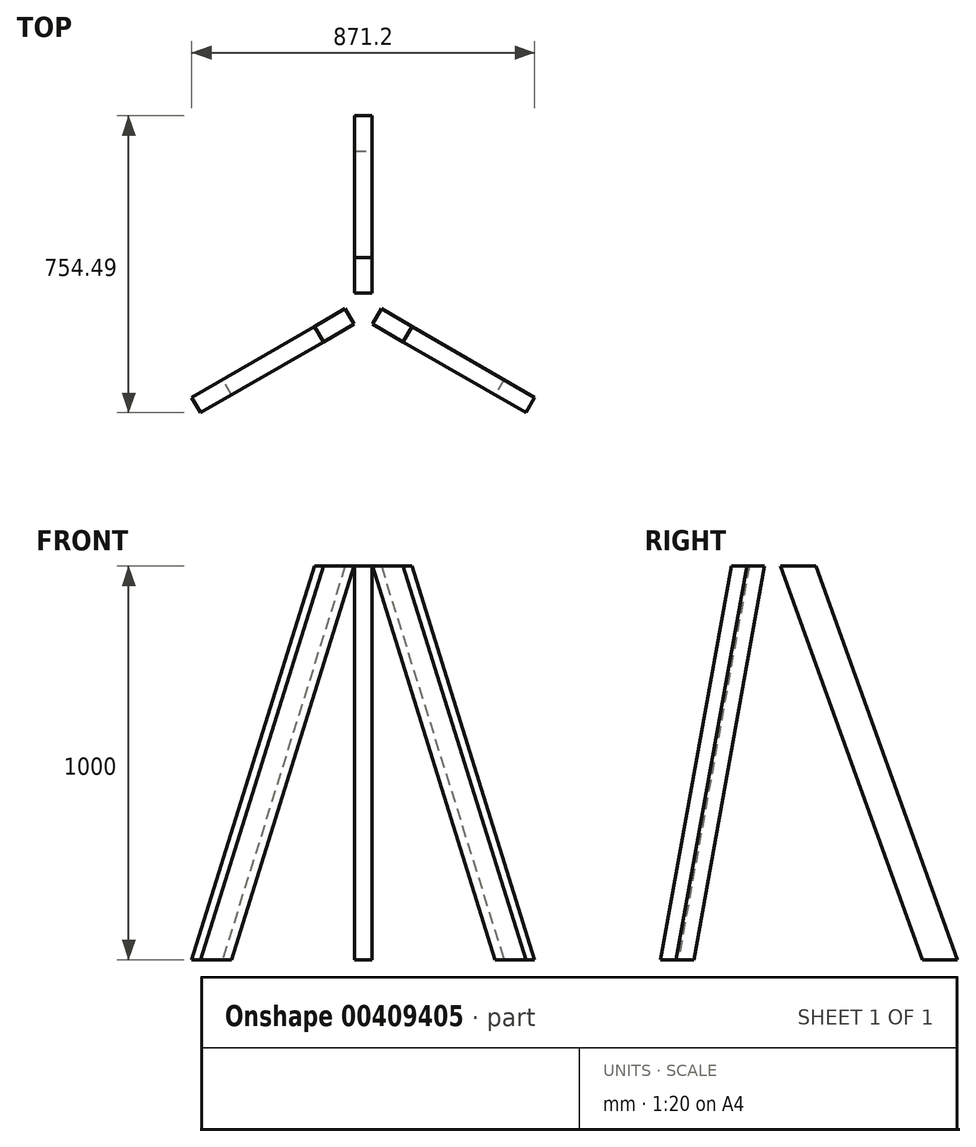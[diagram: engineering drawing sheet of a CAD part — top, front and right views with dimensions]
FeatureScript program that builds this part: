
annotation { "Feature Type Name" : "Feature", "Feature Type Description" : "" }
export const myFeature = defineFeature(function(context is Context, id is Id, definition is map)
    precondition{}
    {
        {
            var Q0;
            Q0=qCreatedBy(makeId("Top.planeOp"),FACE);
            cPlane(context, id + "F0", {"entities" : qUnion([Q0]), "cplaneType" : CPlaneType.OFFSET, "offset" : 25 * mm, "width" : 150 * mm, "height" : 150 * mm});
        }
        {
            var Q0;
            Q0=qCreatedBy(id+"F0.planeOp",FACE);
            var sketch = newSketch(context, id + "F1", { "sketchPlane" : qUnion([Q0])});
            skLineSegment(sketch, "E0.bottom", {"start": v(-22.5, 490) * mm, "end": v(22.5, 490) * mm});
            skLineSegment(sketch, "E0.top", {"start": v(-22.5, 400) * mm, "end": v(22.5, 400) * mm});
            skLineSegment(sketch, "E0.left", {"start": v(-22.5, 490) * mm, "end": v(-22.5, 400) * mm});
            skLineSegment(sketch, "E0.right", {"start": v(22.5, 490) * mm, "end": v(22.5, 400) * mm});
            skLineSegment(sketch, "E1", {"start": v(0, 0) * mm, "end": v(0, 1012.22) * mm, "construction": true});
            skPoint(sketch, "E2.center", {"position": v(0, 506.11) * mm});
            skLineSegment(sketch, "E3.1.0", {"start": v(-435.6, -225.51) * mm, "end": v(-357.66, -180.51) * mm});
            skLineSegment(sketch, "E3.1.1", {"start": v(-413.1, -264.49) * mm, "end": v(-335.16, -219.49) * mm});
            skLineSegment(sketch, "E3.1.2", {"start": v(-413.1, -264.49) * mm, "end": v(-435.6, -225.51) * mm});
            skLineSegment(sketch, "E3.1.3", {"start": v(-335.16, -219.49) * mm, "end": v(-357.66, -180.51) * mm});
            skLineSegment(sketch, "E3.1.4", {"start": v(0, 0) * mm, "end": v(-876.61, -506.11) * mm, "construction": true});
            skLineSegment(sketch, "E3.2.0", {"start": v(413.1, -264.49) * mm, "end": v(335.16, -219.49) * mm});
            skLineSegment(sketch, "E3.2.1", {"start": v(435.6, -225.51) * mm, "end": v(357.66, -180.51) * mm});
            skLineSegment(sketch, "E3.2.2", {"start": v(435.6, -225.51) * mm, "end": v(413.1, -264.49) * mm});
            skLineSegment(sketch, "E3.2.3", {"start": v(357.66, -180.51) * mm, "end": v(335.16, -219.49) * mm});
            skLineSegment(sketch, "E3.2.4", {"start": v(0, 0) * mm, "end": v(876.61, -506.11) * mm, "construction": true});
            skPoint(sketch, "E3.center", {"position": v(0, 0) * mm});
            skSolve(sketch);
        }
        {
            var Q0;
            Q0=qCreatedBy(id+"F0.planeOp",FACE);
            cPlane(context, id + "F2", {"entities" : qUnion([Q0]), "cplaneType" : CPlaneType.OFFSET, "offset" : 1000 * mm, "width" : 150 * mm, "height" : 150 * mm});
        }
        {
            var Q0;
            Q0=qCreatedBy(id+"F2.planeOp",FACE);
            var sketch = newSketch(context, id + "F3", { "sketchPlane" : qUnion([Q0])});
            skLineSegment(sketch, "E4.bottom", {"start": v(-22.5, 130) * mm, "end": v(22.5, 130) * mm});
            skLineSegment(sketch, "E4.top", {"start": v(-22.5, 40) * mm, "end": v(22.5, 40) * mm});
            skLineSegment(sketch, "E4.left", {"start": v(-22.5, 130) * mm, "end": v(-22.5, 40) * mm});
            skLineSegment(sketch, "E4.right", {"start": v(22.5, 130) * mm, "end": v(22.5, 40) * mm});
            skLineSegment(sketch, "E5", {"start": v(0, 0) * mm, "end": v(0, 210.6) * mm, "construction": true});
            skPoint(sketch, "E6.center", {"position": v(0, 0) * mm});
            skLineSegment(sketch, "E7.1.0", {"start": v(-101.33, -84.49) * mm, "end": v(-23.4, -39.49) * mm});
            skLineSegment(sketch, "E7.1.1", {"start": v(-101.33, -84.49) * mm, "end": v(-123.83, -45.51) * mm});
            skLineSegment(sketch, "E7.1.2", {"start": v(-123.83, -45.51) * mm, "end": v(-45.9, -0.51) * mm});
            skLineSegment(sketch, "E7.1.3", {"start": v(-23.4, -39.49) * mm, "end": v(-45.9, -0.51) * mm});
            skLineSegment(sketch, "E7.1.4", {"start": v(0, 0) * mm, "end": v(-182.39, -105.3) * mm, "construction": true});
            skLineSegment(sketch, "E7.2.0", {"start": v(123.83, -45.51) * mm, "end": v(45.9, -0.51) * mm});
            skLineSegment(sketch, "E7.2.1", {"start": v(123.83, -45.51) * mm, "end": v(101.33, -84.49) * mm});
            skLineSegment(sketch, "E7.2.2", {"start": v(101.33, -84.49) * mm, "end": v(23.4, -39.49) * mm});
            skLineSegment(sketch, "E7.2.3", {"start": v(45.9, -0.51) * mm, "end": v(23.4, -39.49) * mm});
            skLineSegment(sketch, "E7.2.4", {"start": v(0, 0) * mm, "end": v(182.39, -105.3) * mm, "construction": true});
            skSolve(sketch);
        }
        {
            var Q0;
            Q0=makeQuery(id+"F3.imprint","IMPRINT",FACE,{"disambiguationData":[TD([[makeQuery(id+"F3.imprint","IMPRINT",EDGE,{"derivedFrom":sQuery(id+"F3.wireOp",EDGE,"E4.bottom")}),-1.0]])]});
            var Q1;
            Q1=makeQuery(id+"F1.imprint","IMPRINT",FACE,{"disambiguationData":[TD([[makeQuery(id+"F1.imprint","IMPRINT",EDGE,{"derivedFrom":sQuery(id+"F1.wireOp",EDGE,"E0.bottom")}),-1.0]])]});
            loft(context, id + "F4", {"sheetProfilesArray" : [{ "sheetProfileEntities" : qUnion([Q0]) }, { "sheetProfileEntities" : qUnion([Q1]) }]});
        }
        {
            var Q0;
            Q0=makeQuery(id+"F3.imprint","IMPRINT",FACE,{"disambiguationData":[TD([[makeQuery(id+"F3.imprint","IMPRINT",EDGE,{"derivedFrom":sQuery(id+"F3.wireOp",EDGE,"E7.2.0")}),1.0]])]});
            var Q1;
            Q1=makeQuery(id+"F1.imprint","IMPRINT",FACE,{"disambiguationData":[TD([[makeQuery(id+"F1.imprint","IMPRINT",EDGE,{"derivedFrom":sQuery(id+"F1.wireOp",EDGE,"E3.2.0")}),-1.0]])]});
            loft(context, id + "F5", {"sheetProfilesArray" : [{ "sheetProfileEntities" : qUnion([Q0]) }, { "sheetProfileEntities" : qUnion([Q1]) }]});
        }
        {
            var Q0;
            Q0=makeQuery(id+"F3.imprint","IMPRINT",FACE,{"disambiguationData":[TD([[makeQuery(id+"F3.imprint","IMPRINT",EDGE,{"derivedFrom":sQuery(id+"F3.wireOp",EDGE,"E7.1.0")}),1.0]])]});
            var Q1;
            Q1=makeQuery(id+"F1.imprint","IMPRINT",FACE,{"disambiguationData":[TD([[makeQuery(id+"F1.imprint","IMPRINT",EDGE,{"derivedFrom":sQuery(id+"F1.wireOp",EDGE,"E3.1.0")}),-1.0]])]});
            loft(context, id + "F6", {"sheetProfilesArray" : [{ "sheetProfileEntities" : qUnion([Q0]) }, { "sheetProfileEntities" : qUnion([Q1]) }]});
        }
    });
